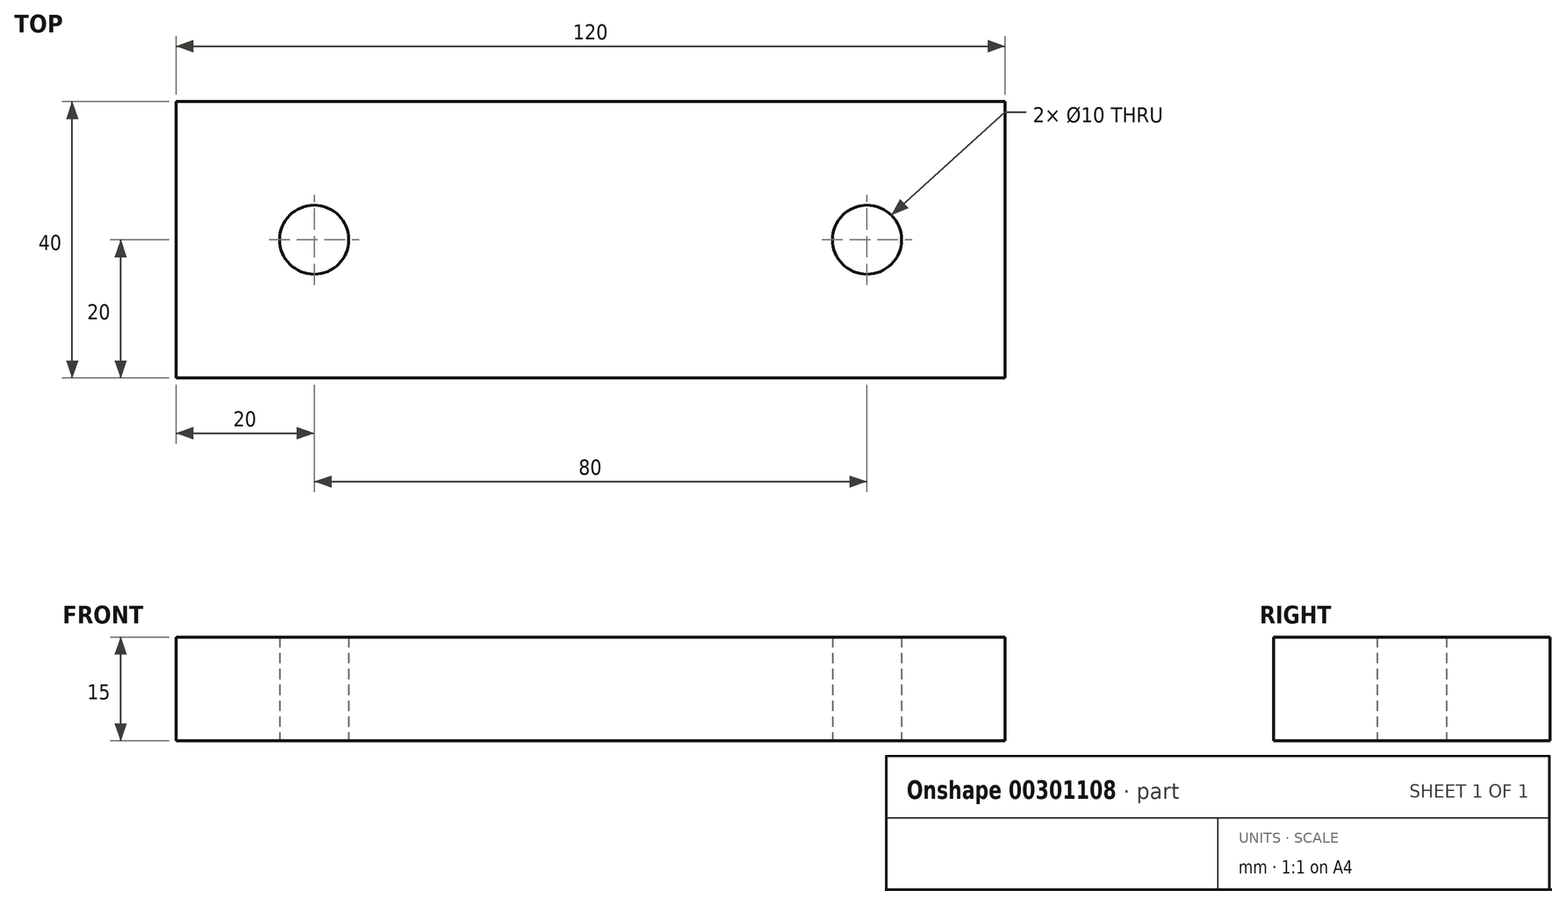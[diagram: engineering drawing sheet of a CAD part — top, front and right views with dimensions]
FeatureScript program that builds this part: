
annotation { "Feature Type Name" : "Feature", "Feature Type Description" : "" }
export const myFeature = defineFeature(function(context is Context, id is Id, definition is map)
    precondition{}
    {
        {
            var Q0;
            Q0=qCreatedBy(makeId("Top.planeOp"),FACE);
            var sketch = newSketch(context, id + "F0", { "sketchPlane" : qUnion([Q0])});
            skLineSegment(sketch, "E0", {"start": v(0, 0) * mm, "end": v(0, 40) * mm});
            skLineSegment(sketch, "E1", {"start": v(0, 40) * mm, "end": v(120, 40) * mm});
            skLineSegment(sketch, "E2", {"start": v(120, 40) * mm, "end": v(120, 0) * mm});
            skLineSegment(sketch, "E3", {"start": v(120, 0) * mm, "end": v(0, 0) * mm});
            skCircle(sketch, "E4", {"center": v(20, 20) * mm, "radius": 5 * mm});
            skCircle(sketch, "E5", {"center": v(100, 20) * mm, "radius": 5 * mm});
            skSolve(sketch);
        }
        {
            var Q0;
            Q0 = qSketchRegion(id + "F0", true);
            extrude(context, id + "F1", {"entities" : qUnion([Q0]), "depth" : 15 * mm});
        }
    });
